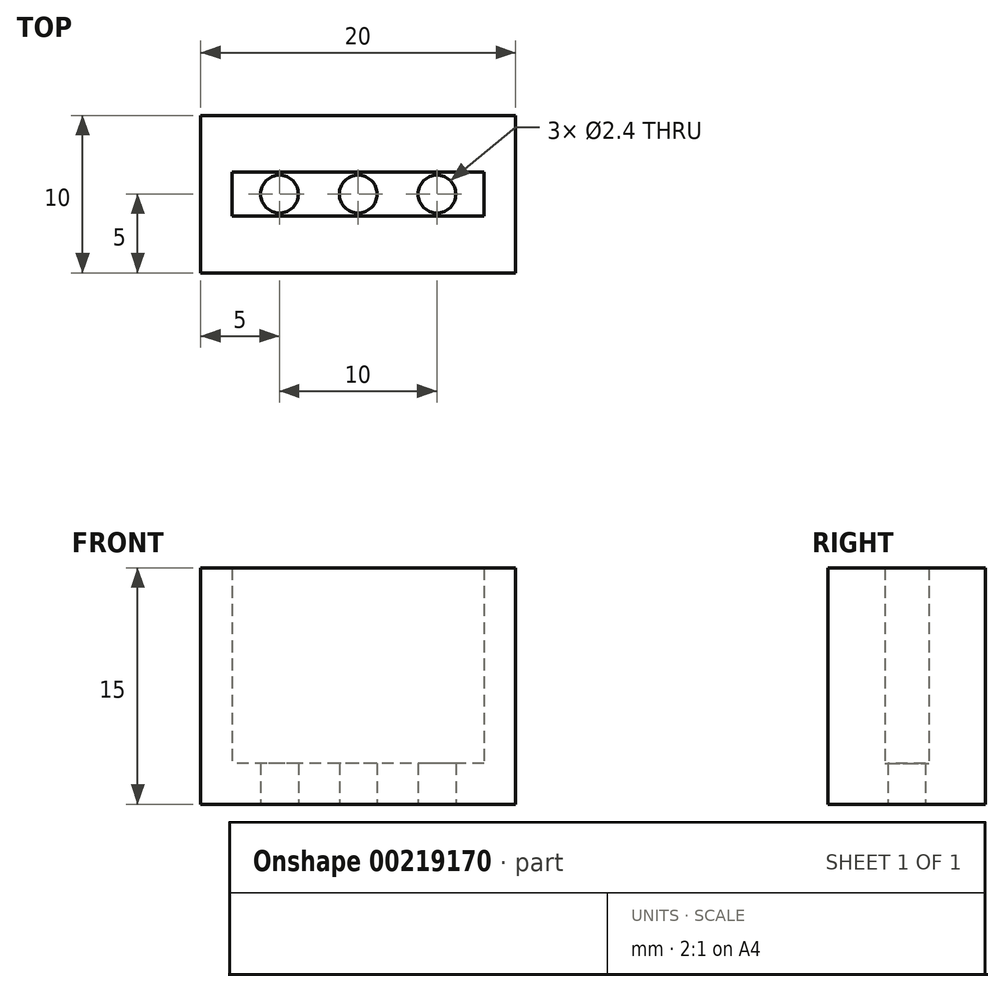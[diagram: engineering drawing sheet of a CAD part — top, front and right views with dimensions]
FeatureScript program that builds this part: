
annotation { "Feature Type Name" : "Feature", "Feature Type Description" : "" }
export const myFeature = defineFeature(function(context is Context, id is Id, definition is map)
    precondition{}
    {
        {
            var Q0;
            Q0=qCreatedBy(makeId("Top.planeOp"),FACE);
            var sketch = newSketch(context, id + "F0", { "sketchPlane" : qUnion([Q0])});
            skCircle(sketch, "E0", {"center": v(0, 0) * mm, "radius": 1.2 * mm});
            skCircle(sketch, "E1.1.0.0", {"center": v(5, 0) * mm, "radius": 1.2 * mm});
            skCircle(sketch, "E1.2.0.0", {"center": v(10, 0) * mm, "radius": 1.2 * mm});
            skLineSegment(sketch, "E1.direction1", {"start": v(0, 0) * mm, "end": v(5, 0) * mm, "construction": true});
            skLineSegment(sketch, "E2.bottom", {"start": v(13, -1.4) * mm, "end": v(-3, -1.4) * mm});
            skLineSegment(sketch, "E2.top", {"start": v(13, 1.4) * mm, "end": v(-3, 1.4) * mm});
            skLineSegment(sketch, "E2.left", {"start": v(13, -1.4) * mm, "end": v(13, 1.4) * mm});
            skLineSegment(sketch, "E2.right", {"start": v(-3, -1.4) * mm, "end": v(-3, 1.4) * mm});
            skLineSegment(sketch, "E3.bottom", {"start": v(15, -5) * mm, "end": v(-5, -5) * mm});
            skLineSegment(sketch, "E3.top", {"start": v(15, 5) * mm, "end": v(-5, 5) * mm});
            skLineSegment(sketch, "E3.left", {"start": v(15, -5) * mm, "end": v(15, 5) * mm});
            skLineSegment(sketch, "E3.right", {"start": v(-5, -5) * mm, "end": v(-5, 5) * mm});
            skSolve(sketch);
        }
        {
            var Q0;
            Q0=makeQuery(id+"F0.imprint","IMPRINT",FACE,{"disambiguationData":[TD([[makeQuery(id+"F0.imprint","IMPRINT",EDGE,{"derivedFrom":sQuery(id+"F0.wireOp",EDGE,"E0")}),-1.0]])]});
            extrude(context, id + "F1", {"entities" : qUnion([Q0]), "depth" : 2.6 * mm});
        }
        {
            var Q0;
            Q0=makeQuery(id+"F0.imprint","IMPRINT",FACE,{"disambiguationData":[TD([[makeQuery(id+"F0.imprint","IMPRINT",EDGE,{"derivedFrom":sQuery(id+"F0.wireOp",EDGE,"E2.bottom")}),1.0]])]});
            extrude(context, id + "F2", {"entities" : qUnion([Q0]), "operationType" : NewBodyOperationType.ADD, "depth" : 15 * mm});
        }
    });
